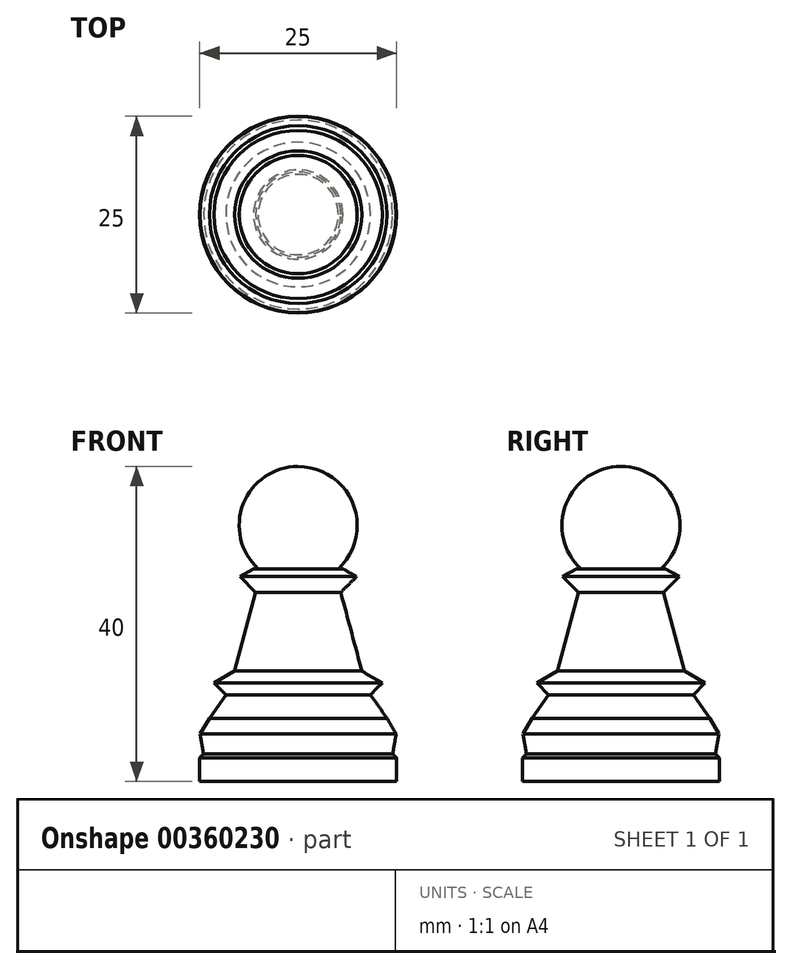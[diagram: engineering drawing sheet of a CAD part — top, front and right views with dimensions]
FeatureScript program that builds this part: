
annotation { "Feature Type Name" : "Feature", "Feature Type Description" : "" }
export const myFeature = defineFeature(function(context is Context, id is Id, definition is map)
    precondition{}
    {
        {
            var Q0;
            Q0=qCreatedBy(makeId("Top.planeOp"),FACE);
            var sketch = newSketch(context, id + "F0", { "sketchPlane" : qUnion([Q0])});
            skCircle(sketch, "E0", {"center": v(0, 0) * mm, "radius": 12.5 * mm});
            skSolve(sketch);
        }
        {
            var Q0;
            Q0=makeQuery(id+"F0.imprint","IMPRINT",FACE,{"disambiguationData":[TD([[makeQuery(id+"F0.imprint","IMPRINT",EDGE,{"derivedFrom":sQuery(id+"F0.wireOp",EDGE,"E0")}),1.0]])]});
            extrude(context, id + "F1", {"entities" : qUnion([Q0]), "depth" : 3 * mm});
        }
        {
            var Q0;
            Q0=makeQuery(id+"F1.opExtrude","CAP_FACE",FACE,{"disambiguationData":[OSD([sQuery(id+"F0.wireOp",EDGE,"E0")])],"isStart":false});
            extrude(context, id + "F2", {"entities" : qUnion([Q0]), "operationType" : NewBodyOperationType.ADD, "depth" : .5 * mm, "hasDraft" : true, "draftAngle" : 45 * degree, "draftPullDirection" : true});
        }
        {
            var Q0;
            Q0=makeQuery(id+"F2.opExtrude","CAP_FACE",FACE,{"disambiguationData":[OSD([sQuery(id+"F0.wireOp",EDGE,"E0")])],"isStart":false});
            extrude(context, id + "F3", {"entities" : qUnion([Q0]), "operationType" : NewBodyOperationType.ADD, "depth" : 2.5 * mm, "hasDraft" : true, "draftAngle" : 10 * degree});
        }
        {
            var Q0;
            Q0=makeQuery(id+"F3.opExtrude","CAP_FACE",FACE,{"disambiguationData":[OSD([sQuery(id+"F0.wireOp",EDGE,"E0")])],"isStart":false});
            extrude(context, id + "F4", {"entities" : qUnion([Q0]), "operationType" : NewBodyOperationType.ADD, "depth" : 2 * mm, "hasDraft" : true, "draftAngle" : 30 * degree, "draftPullDirection" : true});
        }
        {
            var Q0;
            Q0=makeQuery(id+"F4.opExtrude","CAP_FACE",FACE,{"disambiguationData":[OSD([sQuery(id+"F0.wireOp",EDGE,"E0")])],"isStart":false});
            extrude(context, id + "F5", {"entities" : qUnion([Q0]), "operationType" : NewBodyOperationType.ADD, "depth" : 3 * mm, "hasDraft" : true, "draftAngle" : 35 * degree, "draftPullDirection" : true});
        }
        {
            var Q0;
            Q0=makeQuery(id+"F5.opExtrude","CAP_FACE",FACE,{"disambiguationData":[OSD([sQuery(id+"F0.wireOp",EDGE,"E0")])],"isStart":false});
            extrude(context, id + "F6", {"entities" : qUnion([Q0]), "operationType" : NewBodyOperationType.ADD, "depth" : 1.5 * mm, "hasDraft" : true, "draftAngle" : 45 * degree});
        }
        {
            var Q0;
            Q0=makeQuery(id+"F6.opExtrude","CAP_FACE",FACE,{"disambiguationData":[OSD([sQuery(id+"F0.wireOp",EDGE,"E0")])],"isStart":false});
            extrude(context, id + "F7", {"entities" : qUnion([Q0]), "operationType" : NewBodyOperationType.ADD, "depth" : 1.5 * mm, "hasDraft" : true, "draftAngle" : 60 * degree, "draftPullDirection" : true});
        }
        {
            var Q0;
            Q0=makeQuery(id+"F7.opExtrude","CAP_FACE",FACE,{"disambiguationData":[OSD([sQuery(id+"F0.wireOp",EDGE,"E0")])],"isStart":false});
            extrude(context, id + "F8", {"entities" : qUnion([Q0]), "operationType" : NewBodyOperationType.ADD, "depth" : 10 * mm, "hasDraft" : true, "draftAngle" : 15 * degree, "draftPullDirection" : true});
        }
        {
            var Q0;
            Q0=makeQuery(id+"F8.opExtrude","CAP_FACE",FACE,{"disambiguationData":[OSD([sQuery(id+"F0.wireOp",EDGE,"E0")])],"isStart":false});
            extrude(context, id + "F9", {"entities" : qUnion([Q0]), "operationType" : NewBodyOperationType.ADD, "depth" : 2 * mm, "hasDraft" : true, "draftAngle" : 45 * degree});
        }
        {
            var Q0;
            Q0=makeQuery(id+"F9.opExtrude","CAP_FACE",FACE,{"disambiguationData":[OSD([sQuery(id+"F0.wireOp",EDGE,"E0")])],"isStart":false});
            extrude(context, id + "F10", {"entities" : qUnion([Q0]), "operationType" : NewBodyOperationType.ADD, "depth" : 1 * mm, "hasDraft" : true, "draftAngle" : 60 * degree, "draftPullDirection" : true});
        }
        {
            var Q0;
            Q0=qCreatedBy(makeId("Front.planeOp"),FACE);
            var sketch = newSketch(context, id + "F11", { "sketchPlane" : qUnion([Q0])});
            skLineSegment(sketch, "E1", {"start": v(0, 0) * mm, "end": v(0, 42) * mm});
            skCircle(sketch, "E2", {"center": v(0, 32.5) * mm, "radius": 7.5 * mm});
            skSolve(sketch);
        }
        {
            var Q0;
            {var subQ0=sQuery(id+"F11.wireOp",EDGE,"E2");var subQ1=sQuery(id+"F11.wireOp",EDGE,"E1");var subQ2=makeQuery(id+"F11.imprint","INTERSECT",VERTEX,{"disambiguationData":[OD(0.0)],"derivedFrom":[subQ1,subQ0]});Q0=makeQuery(id+"F11.imprint","IMPRINT",FACE,{"disambiguationData":[TD([[makeQuery(id+"F11.imprint","IMPRINT",EDGE,{"disambiguationData":[TD([[subQ2,-1.0]])],"derivedFrom":subQ1}),1.0]])]});}
            var Q1;
            Q1=sQuery(id+"F11.wireOp",EDGE,"E1");
            revolve(context, id + "F12", {"operationType" : NewBodyOperationType.ADD, "entities" : qUnion([Q0]), "axis" : qUnion([Q1]), "revolveType" : RevolveType.FULL});
        }
    });
